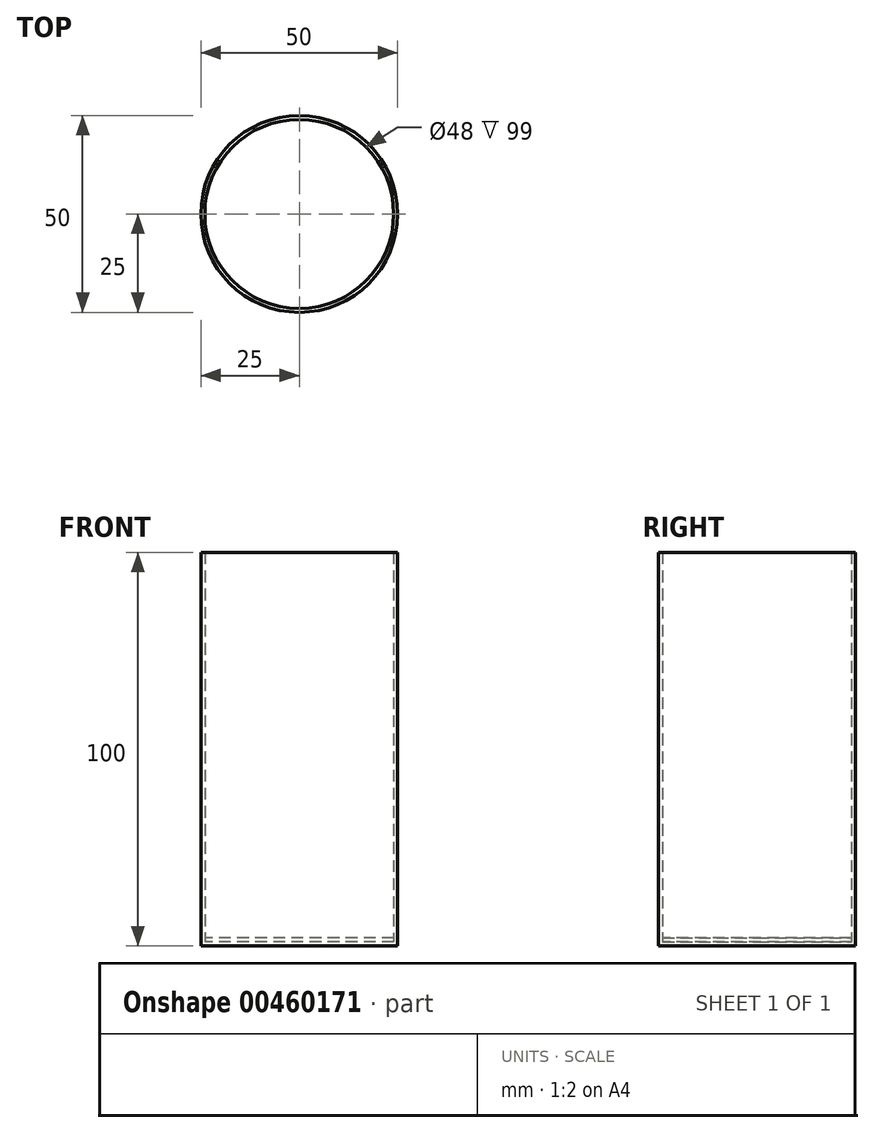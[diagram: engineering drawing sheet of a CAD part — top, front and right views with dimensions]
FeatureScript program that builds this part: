
annotation { "Feature Type Name" : "Feature", "Feature Type Description" : "" }
export const myFeature = defineFeature(function(context is Context, id is Id, definition is map)
    precondition{}
    {
        {
            var Q0;
            Q0=qCreatedBy(makeId("Top.planeOp"),FACE);
            var sketch = newSketch(context, id + "F0", { "sketchPlane" : qUnion([Q0])});
            skCircle(sketch, "E0", {"center": v(0, 0) * mm, "radius": 25 * mm});
            skSolve(sketch);
        }
        {
            var Q0;
            Q0=makeQuery(id+"F0.imprint","IMPRINT",FACE,{"disambiguationData":[TD([[makeQuery(id+"F0.imprint","IMPRINT",EDGE,{"derivedFrom":sQuery(id+"F0.wireOp",EDGE,"E0")}),1.0]])]});
            extrude(context, id + "F1", {"entities" : qUnion([Q0]), "depth" : 100 * mm});
        }
        {
            var Q0;
            Q0=makeQuery(id+"F1.opExtrude","CAP_FACE",FACE,{"disambiguationData":[OSD([sQuery(id+"F0.wireOp",EDGE,"E0")])],"isStart":false});
            shell(context, id + "F2", {"entities" : qUnion([Q0]), "thickness" : 1 * mm});
        }
        {
            var Q0;
            {var subQ0=sQuery(id+"F0.wireOp",EDGE,"E0");Q0=makeQuery(id+"F2.opShell","OFFSET_FACE",FACE,{"disambiguationData":[OSD([subQ0]),TDD([makeQuery(id+"F1.opExtrude","CAP_FACE",FACE,{"disambiguationData":[OSD([subQ0])],"isStart":true})])]});}
            extrude(context, id + "F3", {"entities" : qUnion([Q0]), "depth" : 1 * mm});
        }
        {
            var Q0;
            Q0=qCreatedBy(makeId("Front.planeOp"),FACE);
            var sketch = newSketch(context, id + "F4", { "sketchPlane" : qUnion([Q0])});
            skLineSegment(sketch, "E1.bottom", {"start": v(1.5, 2.52) * mm, "end": v(-1.5, 2.52) * mm});
            skLineSegment(sketch, "E1.top", {"start": v(1.5, 5.52) * mm, "end": v(-1.5, 5.52) * mm});
            skLineSegment(sketch, "E1.left", {"start": v(1.5, 2.52) * mm, "end": v(1.5, 5.52) * mm});
            skLineSegment(sketch, "E1.right", {"start": v(-1.5, 2.52) * mm, "end": v(-1.5, 5.52) * mm});
            skPoint(sketch, "E1.middle", {"position": v(0, 4.02) * mm});
            skSolve(sketch);
        }
        {
            var Q0;
            Q0=makeQuery(id+"F4.imprint","IMPRINT",FACE,{"disambiguationData":[TD([[makeQuery(id+"F4.imprint","IMPRINT",EDGE,{"derivedFrom":sQuery(id+"F4.wireOp",EDGE,"E1.bottom")}),-1.0]])]});
            extrude(context, id + "F5", {"entities" : qUnion([Q0]), "operationType" : NewBodyOperationType.ADD, "depth" : 5 * mm});
        }
        {
            var Q0;
            Q0=makeQuery(id+"F5.opExtrude","SWEPT_BODY",BODY,{"disambiguationData":[OSD([sQuery(id+"F4.wireOp",EDGE,"E1.bottom"),sQuery(id+"F4.wireOp",EDGE,"E1.top"),sQuery(id+"F4.wireOp",EDGE,"E1.left"),sQuery(id+"F4.wireOp",EDGE,"E1.right")])]});
            deleteBodies(context, id + "F6", {"entities" : qUnion([Q0])});
        }
    });
